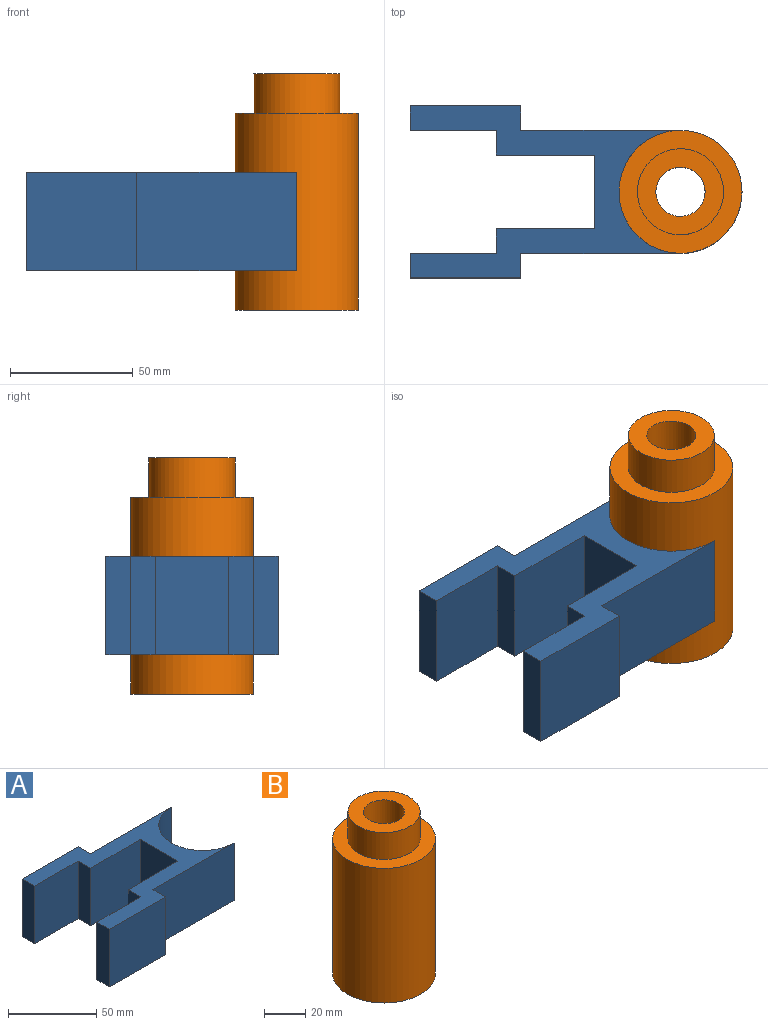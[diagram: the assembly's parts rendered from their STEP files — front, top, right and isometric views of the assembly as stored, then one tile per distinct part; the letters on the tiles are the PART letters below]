
ASSEMBLY  parts=2 mates=1
PART A: 18 faces, bbox 110x70x40 mm
  f0: plane 40x35mm, normal (0,-1,0), area 1400mm2, adj f1,f15,f16,f17
  f1: plane 40x10mm, normal (-1,0,0), area 400mm2, adj f0,f2,f16,f17
  f2: plane 40x40mm, normal (0,-1,0), area 1600mm2, adj f1,f3,f16,f17
  f3: plane 40x30mm, normal (-1,0,0), area 1200mm2, adj f2,f4,f16,f17
  f4: plane 40x40mm, normal (0,1,0), area 1600mm2, adj f3,f5,f16,f17
  f5: plane 40x10mm, normal (-1,0,0), area 400mm2, adj f4,f6,f16,f17
  f6: plane 40x35mm, normal (0,1,0), area 1400mm2, adj f5,f7,f16,f17
  f7: plane 40x10mm, normal (-1,0,0), area 400mm2, adj f6,f8,f16,f17
  f8: plane 45x40mm, normal (0,-1,0), area 1800mm2, adj f7,f9,f16,f17
  f9: plane 40x10mm, normal (1,0,0), area 400mm2, adj f8,f10,f16,f17
  f10: plane 65x40mm, normal (0,-1,0), area 2600mm2, adj f9,f11,f16,f17
  f11: cylinder r=25mm len=50mm, axis (0,0,-1), area 3141.6mm2, adj f10,f12,f16,f17
  f12: plane 65x40mm, normal (0,1,0), area 2600mm2, adj f11,f13,f16,f17
  f13: plane 40x10mm, normal (1,0,0), area 400mm2, adj f12,f14,f16,f17
  f14: plane 45x40mm, normal (0,1,0), area 1800mm2, adj f13,f15,f16,f17
  f15: plane 40x10mm, normal (-1,0,0), area 400mm2, adj f0,f14,f16,f17
  f16: plane 110x70mm, normal (0,0,1), area 2468.3mm2, adj f0,f1,f2,f3,f4,f5,f6,f7
  f17: plane 110x70mm, normal (0,0,-1), area 2468.3mm2, adj f0,f1,f2,f3,f4,f5,f6,f7
PART B: 8 faces, bbox 50x50x96 mm
  f0: cylinder r=17.5mm len=35mm, axis (0,0,1), area 1759.3mm2, adj f2,f7
  f1: cylinder r=25mm len=80mm, axis (0,0,1), area 12566.4mm2, adj f2,f3
  f2: plane 50x50mm, normal (0,0,-1), area 1001.4mm2, adj f0,f1
  f3: plane 50x50mm, normal (0,0,1), area 1001.4mm2, adj f1,f5
  f4: cylinder r=10mm len=80mm, axis (0,0,-1), area 5026.5mm2, adj f6,f7
  f5: cylinder r=17.5mm len=35mm, axis (0,0,-1), area 1759.3mm2, adj f3,f6
  f6: plane 35x35mm, normal (0,0,1), area 648mm2, adj f4,f5
  f7: plane 35x35mm, normal (0,0,-1), area 648mm2, adj f0,f4
PLACE A at identity
PLACE B t=(110,35,0)mm
MATE fastened B.f4 <-> A.f11  axis (0,0,-1) through (110,35,0)mm
